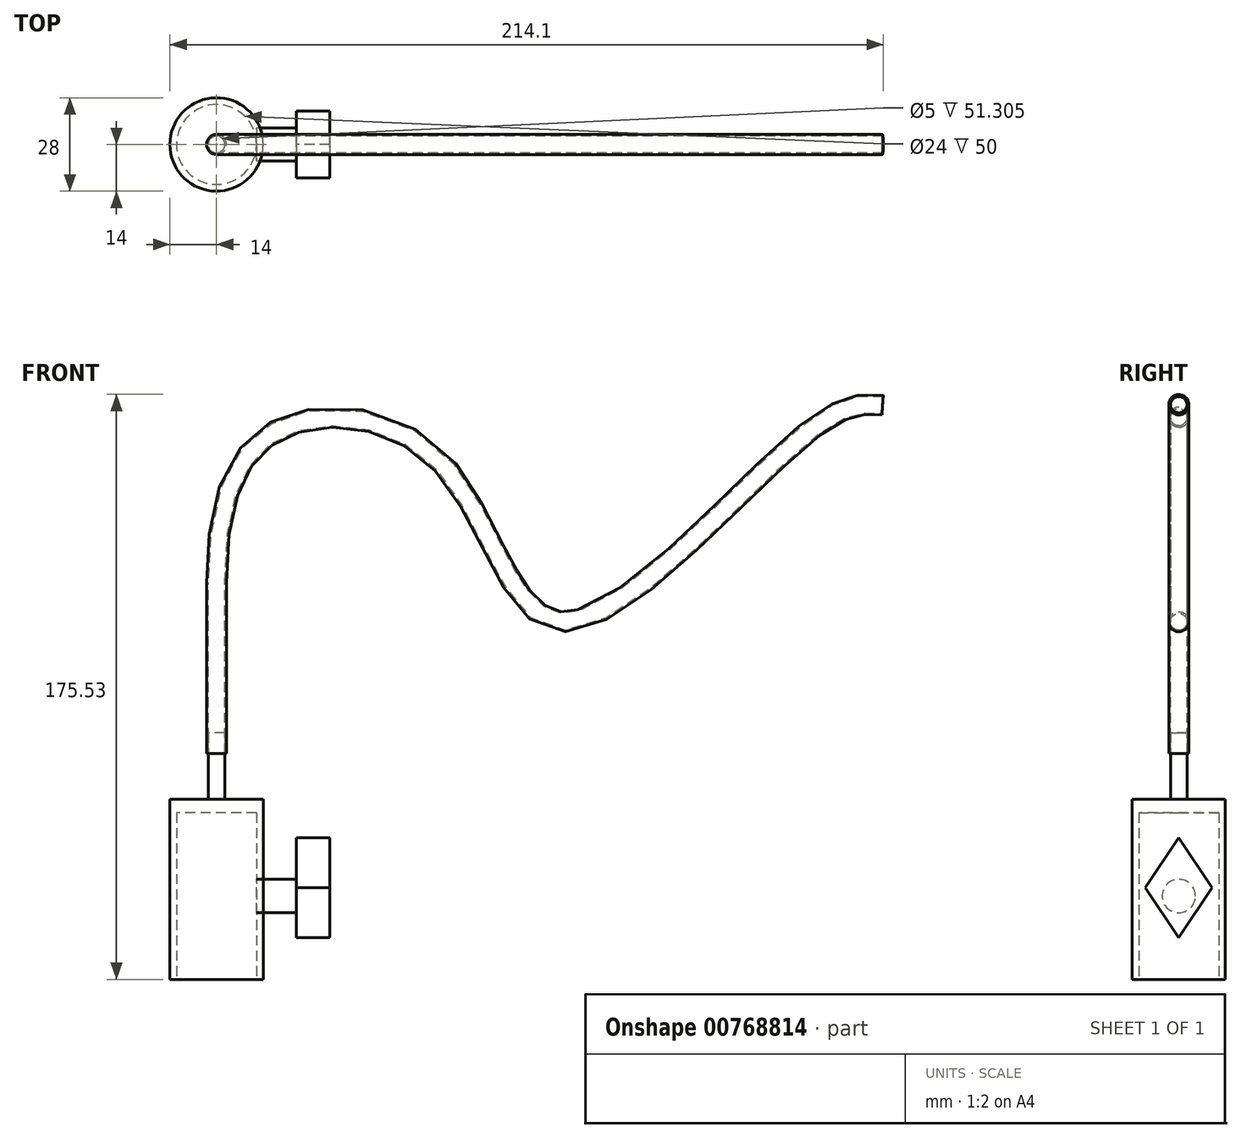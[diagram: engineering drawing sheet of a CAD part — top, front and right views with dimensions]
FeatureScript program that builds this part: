
annotation { "Feature Type Name" : "Feature", "Feature Type Description" : "" }
export const myFeature = defineFeature(function(context is Context, id is Id, definition is map)
    precondition{}
    {
        {
            var Q0;
            Q0=qCreatedBy(makeId("Top.planeOp"),FACE);
            var sketch = newSketch(context, id + "F0", { "sketchPlane" : qUnion([Q0])});
            skCircle(sketch, "E0", {"center": v(0, 0) * mm, "radius": 7 * mm});
            skSolve(sketch);
        }
        {
            var Q0;
            Q0=makeQuery(id+"FSjPhCLkiX47vxu_1.imprint","IMPRINT",FACE,{"disambiguationData":[TD([[makeQuery(id+"FSjPhCLkiX47vxu_1.imprint","IMPRINT",EDGE,{"derivedFrom":sQuery(id+"FSjPhCLkiX47vxu_1.wireOp",EDGE,"A87imJcb-5fSZ-l6N6-1vi1-vgmKPIcJpidu")}),1.0]])]});
            var Q1;
            Q1=makeQuery(id+"F0.imprint","IMPRINT",FACE,{"disambiguationData":[TD([[makeQuery(id+"F0.imprint","IMPRINT",EDGE,{"derivedFrom":sQuery(id+"F0.wireOp",EDGE,"E0")}),1.0]])]});
            var Q2;
            Q2=sQuery(id+"F0.wireOp",EDGE,"E0");
            extrude(context, id + "F1", {"entities" : qUnion([Q0, Q1]), "surfaceEntities" : qUnion([Q2]), "depth" : 25 * mm, "offsetDistance" : 25 * mm});
        }
        {
            var Q0;
            Q0=qCreatedBy(makeId("Top.planeOp"),FACE);
            var sketch = newSketch(context, id + "F2", { "sketchPlane" : qUnion([Q0])});
            skCircle(sketch, "E1", {"center": v(0, 0) * mm, "radius": 6 * mm});
            skSolve(sketch);
        }
        {
            var Q0;
            Q0=makeQuery(id+"F2.imprint","IMPRINT",FACE,{"disambiguationData":[TD([[makeQuery(id+"F2.imprint","IMPRINT",EDGE,{"derivedFrom":sQuery(id+"F2.wireOp",EDGE,"E1")}),1.0]])]});
            extrude(context, id + "F3", {"entities" : qUnion([Q0]), "operationType" : NewBodyOperationType.REMOVE, "depth" : 25 * mm, "offsetDistance" : 25 * mm});
        }
        {
            var Q0;
            Q0=qCreatedBy(makeId("Front.planeOp"),FACE);
            var sketch = newSketch(context, id + "F4", { "sketchPlane" : qUnion([Q0])});
            skLineSegment(sketch, "E2", {"start": v(0, 0) * mm, "end": v(0, 12.5) * mm, "construction": true});
            skLineSegment(sketch, "E3", {"start": v(0, 12.5) * mm, "end": v(7, 12.5) * mm, "construction": true});
            skPoint(sketch, "E4", {"position": v(7, 12.5) * mm});
            skSolve(sketch);
        }
        {
            var Q0;
            Q0=sQuery(id+"F4.wireOp",VERTEX,"E4");
            var Q1;
            Q1=qCreatedBy(makeId("Right.planeOp"),FACE);
            cPlane(context, id + "F5", {"entities" : qUnion([Q0, Q1]), "cplaneType" : CPlaneType.PLANE_POINT, "offset" : 25 * mm, "width" : 150 * mm, "height" : 150 * mm});
        }
        {
            var Q0;
            Q0=qCreatedBy(id+"F5.planeOp",FACE);
            var sketch = newSketch(context, id + "F6", { "sketchPlane" : qUnion([Q0])});
            skLineSegment(sketch, "E5", {"start": v(0, 0) * mm, "end": v(0, 12.5) * mm, "construction": true});
            skCircle(sketch, "E6", {"center": v(0, 12.5) * mm, "radius": 2.5 * mm});
            skSolve(sketch);
        }
        {
            var Q0;
            Q0 = qSketchRegion(id + "F6", true);
            var Q1;
            Q1=sQuery(id+"F6.wireOp",EDGE,"E6");
            extrude(context, id + "F7", {"entities" : qUnion([Q0]), "surfaceEntities" : qUnion([Q1]), "depth" : 5 * mm, "offsetDistance" : 25 * mm, "hasSecondDirection" : true, "secondDirectionOppositeDirection" : true, "secondDirectionDepth" : 1 * mm});
        }
        {
            var Q0;
            Q0=qCreatedBy(id+"F5.planeOp",FACE);
            cPlane(context, id + "F8", {"entities" : qUnion([Q0]), "cplaneType" : CPlaneType.OFFSET, "offset" : 5 * mm, "width" : 150 * mm, "height" : 150 * mm});
        }
        {
            var Q0;
            Q0=qCreatedBy(id+"F8.planeOp",FACE);
            var sketch = newSketch(context, id + "F9", { "sketchPlane" : qUnion([Q0])});
            skPoint(sketch, "E7", {"position": v(-5, 12.5) * mm});
            skPoint(sketch, "E8", {"position": v(5, 12.5) * mm});
            skLineSegment(sketch, "E9", {"start": v(0, 20) * mm, "end": v(-5, 12.5) * mm});
            skLineSegment(sketch, "E10", {"start": v(-5, 12.5) * mm, "end": v(0, 5) * mm});
            skLineSegment(sketch, "E11", {"start": v(0, 5) * mm, "end": v(5, 12.5) * mm});
            skLineSegment(sketch, "E12", {"start": v(5, 12.5) * mm, "end": v(0, 20) * mm});
            skPoint(sketch, "E13.center.orphan", {"position": v(0, 17.5) * mm});
            skPoint(sketch, "E14.orphan", {"position": v(0, 7.5) * mm});
            skSolve(sketch);
        }
        {
            var Q0;
            Q0 = qSketchRegion(id + "F9", true);
            extrude(context, id + "F10", {"entities" : qUnion([Q0]), "depth" : 5 * mm, "offsetDistance" : 25 * mm});
        }
        {
            var Q0;
            Q0=qCreatedBy(makeId("Top.planeOp"),FACE);
            cPlane(context, id + "F11", {"entities" : qUnion([Q0]), "cplaneType" : CPlaneType.OFFSET, "offset" : 25 * mm, "width" : 150 * mm, "height" : 150 * mm});
        }
        {
            var Q0;
            Q0=qCreatedBy(id+"F11.planeOp",FACE);
            var sketch = newSketch(context, id + "F12", { "sketchPlane" : qUnion([Q0])});
            skCircle(sketch, "E15", {"center": v(0, 0) * mm, "radius": 7 * mm});
            skSolve(sketch);
        }
        {
            var Q0;
            Q0 = qSketchRegion(id + "F12", true);
            extrude(context, id + "F13", {"entities" : qUnion([Q0]), "operationType" : NewBodyOperationType.ADD, "depth" : 2 * mm, "offsetDistance" : 25 * mm});
        }
        {
            var Q0;
            Q0=makeQuery(id+"F13.opExtrude","CAP_FACE",FACE,{"disambiguationData":[OSD([sQuery(id+"F12.wireOp",EDGE,"E15")])],"isStart":false});
            cPlane(context, id + "F14", {"entities" : qUnion([Q0]), "cplaneType" : CPlaneType.OFFSET, "offset" : 0 * mm, "width" : 150 * mm, "height" : 150 * mm});
        }
        {
            var Q0;
            Q0=qCreatedBy(id+"F14.planeOp",FACE);
            var sketch = newSketch(context, id + "F15", { "sketchPlane" : qUnion([Q0])});
            skCircle(sketch, "E16", {"center": v(0, 0) * mm, "radius": 1.25 * mm});
            skSolve(sketch);
        }
        {
            var Q0;
            Q0 = qSketchRegion(id + "F15", true);
            extrude(context, id + "F16", {"entities" : qUnion([Q0]), "operationType" : NewBodyOperationType.ADD, "depth" : 10 * mm, "offsetDistance" : 25 * mm});
        }
        {
            var Q0;
            Q0=qCreatedBy(id+"F14.planeOp",FACE);
            cPlane(context, id + "F17", {"entities" : qUnion([Q0]), "cplaneType" : CPlaneType.OFFSET, "offset" : 5 * mm, "width" : 150 * mm, "height" : 150 * mm});
        }
        {
            var Q0;
            Q0=qCreatedBy(makeId("Front.planeOp"),FACE);
            var sketch = newSketch(context, id + "F18", { "sketchPlane" : qUnion([Q0])});
            skPoint(sketch, "E17", {"position": v(9.43, 79.8) * mm});
            skPoint(sketch, "E18", {"position": v(33.77, 74.76) * mm});
            skPoint(sketch, "E19", {"position": v(51.71, 50.92) * mm});
            skPoint(sketch, "E20", {"position": v(89.24, 80.62) * mm});
            skLineSegment(sketch, "E21", {"start": v(0, 31.16) * mm, "end": v(0, 56.8) * mm});
            skFitSpline(sketch, "E22", {"points": [v(0, 56.8) * mm, v(9.43, 79.8) * mm, v(33.77, 74.76) * mm, v(51.71, 50.92) * mm, v(90.34, 80.62) * mm, v(99.95, 83.43) * mm], "startDerivative": vector(0, 184.77) * mm, "endDerivative": vector(62.7, -4.34) * mm});
            skSolve(sketch);
        }
        {
            var Q0;
            Q0=qCreatedBy(id+"F17.planeOp",FACE);
            var sketch = newSketch(context, id + "F19", { "sketchPlane" : qUnion([Q0])});
            skCircle(sketch, "E23", {"center": v(0, 0) * mm, "radius": 1.5 * mm});
            skCircle(sketch, "E24", {"center": v(0, 0) * mm, "radius": 1.25 * mm});
            skSolve(sketch);
        }
        {
            var Q0;
            Q0=makeQuery(id+"F19.imprint","IMPRINT",FACE,{"disambiguationData":[TD([[makeQuery(id+"F19.imprint","IMPRINT",EDGE,{"derivedFrom":sQuery(id+"F19.wireOp",EDGE,"E23")}),1.0]])]});
            var Q1;
            Q1 = qConstructionFilter(qBodyType(qCreatedBy(id + "F18" ,EDGE), BodyType.WIRE), ConstructionObject.NO);
            sweep(context, id + "F20", {"profiles" : qUnion([Q0]), "path" : qUnion([Q1])});
        }
        {
            var Q0;
            Q0=makeQuery(id+"F1.opExtrude","SWEPT_BODY",BODY,{"disambiguationData":[OSD([sQuery(id+"F0.wireOp",EDGE,"E0")])]});
            var Q1;
            Q1=sQuery(id+"F4.wireOp",VERTEX,"E2.end");
            transform(context, id + "F21", {"entities" : qUnion([Q0]), "transformType" : TransformType.SCALE_UNIFORMLY, "scale" : 2, "scalePoint" : qUnion([Q1]), "makeCopy" : false});
        }
        {
            var Q0;
            Q0=makeQuery(id+"F20.opSweep","SWEPT_BODY",BODY,{"disambiguationData":[OSD([sQuery(id+"F18.wireOp",EDGE,"E22"),sQuery(id+"F19.wireOp",EDGE,"E23"),sQuery(id+"F19.wireOp",EDGE,"E24")])]});
            var Q1;
            Q1=sQuery(id+"F15.wireOp",VERTEX,"E16.center");
            transform(context, id + "F22", {"entities" : qUnion([Q0]), "transformType" : TransformType.SCALE_UNIFORMLY, "scale" : 2, "scalePoint" : qUnion([Q1]), "makeCopy" : false});
        }
        {
            var Q0;
            Q0=makeQuery(id+"F20.opSweep","SWEPT_BODY",BODY,{"disambiguationData":[OSD([sQuery(id+"F18.wireOp",EDGE,"E22"),sQuery(id+"F19.wireOp",EDGE,"E23"),sQuery(id+"F19.wireOp",EDGE,"E24")])]});
            transform(context, id + "F23", {"entities" : qUnion([Q0]), "transformType" : TransformType.TRANSLATION_3D, "dx" : 0 * mm, "dy" : 0 * mm, "dz" : 20 * mm, "makeCopy" : false});
        }
        {
            var Q0;
            Q0=makeQuery(id+"F10.opExtrude","SWEPT_BODY",BODY,{"disambiguationData":[OSD([sQuery(id+"F9.wireOp",EDGE,"E9"),sQuery(id+"F9.wireOp",EDGE,"E10"),sQuery(id+"F9.wireOp",EDGE,"E11"),sQuery(id+"F9.wireOp",EDGE,"E12")])]});
            transform(context, id + "F24", {"entities" : qUnion([Q0]), "transformType" : TransformType.TRANSLATION_3D, "dx" : 10 * mm, "dy" : 0 * mm, "dz" : 0 * mm, "makeCopy" : false});
        }
        {
            var Q0;
            Q0=makeQuery(id+"F7.opExtrude","SWEPT_BODY",BODY,{"disambiguationData":[OSD([sQuery(id+"F6.wireOp",EDGE,"E6")])]});
            var Q1;
            Q1=qCreatedBy(makeId("Origin.pointOp"),VERTEX);
            transform(context, id + "F25", {"entities" : qUnion([Q0]), "transformType" : TransformType.SCALE_UNIFORMLY, "scale" : 2, "scalePoint" : qUnion([Q1]), "makeCopy" : false});
        }
        {
            var Q0;
            Q0=makeQuery(id+"F7.opExtrude","SWEPT_BODY",BODY,{"disambiguationData":[OSD([sQuery(id+"F6.wireOp",EDGE,"E6")])]});
            transform(context, id + "F26", {"entities" : qUnion([Q0]), "transformType" : TransformType.TRANSLATION_3D, "dx" : 0 * mm, "dy" : 0 * mm, "dz" : -12.5 * mm, "makeCopy" : false});
        }
        {
            var Q0;
            Q0=makeQuery(id+"F10.opExtrude","SWEPT_BODY",BODY,{"disambiguationData":[OSD([sQuery(id+"F9.wireOp",EDGE,"E9"),sQuery(id+"F9.wireOp",EDGE,"E10"),sQuery(id+"F9.wireOp",EDGE,"E11"),sQuery(id+"F9.wireOp",EDGE,"E12")])]});
            var Q1;
            Q1=qCreatedBy(makeId("Origin.pointOp"),VERTEX);
            transform(context, id + "F27", {"entities" : qUnion([Q0]), "transformType" : TransformType.SCALE_UNIFORMLY, "scale" : 2, "scalePoint" : qUnion([Q1]), "makeCopy" : false});
        }
        {
            var Q0;
            Q0=makeQuery(id+"F10.opExtrude","SWEPT_BODY",BODY,{"disambiguationData":[OSD([sQuery(id+"F9.wireOp",EDGE,"E9"),sQuery(id+"F9.wireOp",EDGE,"E10"),sQuery(id+"F9.wireOp",EDGE,"E11"),sQuery(id+"F9.wireOp",EDGE,"E12")])]});
            transform(context, id + "F28", {"entities" : qUnion([Q0]), "transformType" : TransformType.TRANSLATION_3D, "dx" : -20 * mm, "dy" : 0 * mm, "dz" : -10 * mm, "makeCopy" : false});
        }
    });
